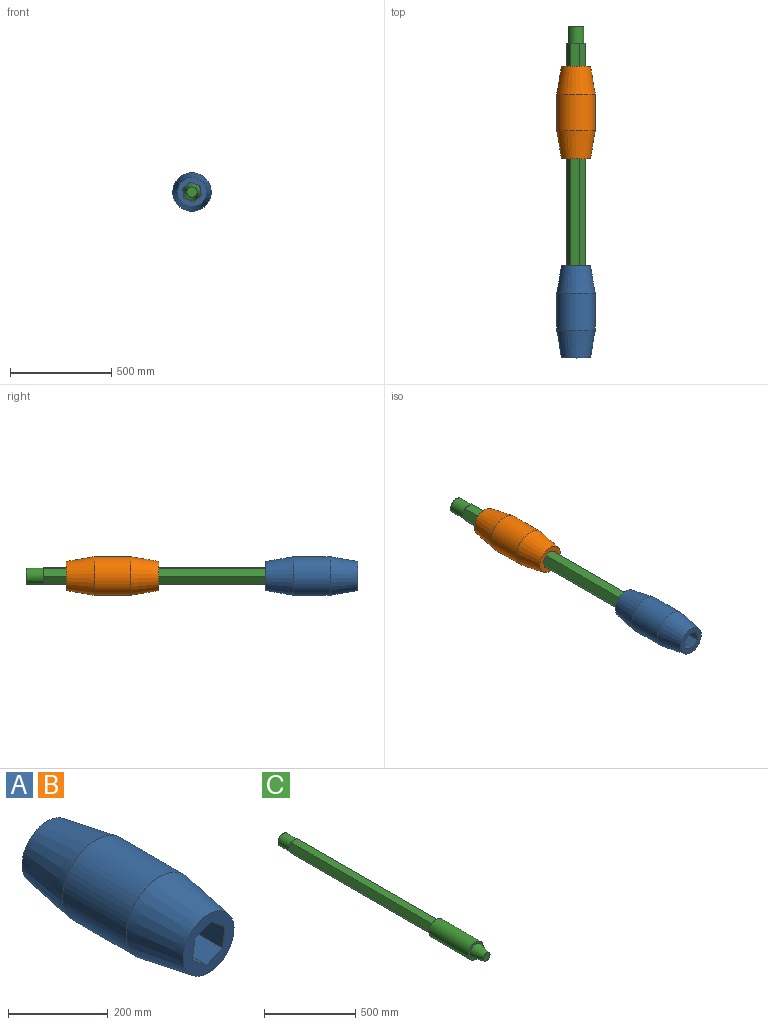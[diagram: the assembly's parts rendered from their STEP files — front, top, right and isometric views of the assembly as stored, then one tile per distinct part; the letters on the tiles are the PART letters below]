
ASSEMBLY  parts=3 mates=2
PART A: 11 faces, bbox 190.5x457.2x190.5 mm
  f0: plane 144.08x144.08mm, normal (0,1,0), area 9802.4mm2, adj f1,f5,f6,f7,f8,f9,f10
  f1: cone r=95.25mm half-angle=9.5deg, axis (0,-1,0), area 73644.5mm2, adj f0,f2
  f2: cylinder r=95.25mm len=190.5mm, axis (0,-1,0), area 108215.6mm2, adj f1,f3
  f3: cone r=95.25mm half-angle=9.5deg, axis (0,1,0), area 73644.5mm2, adj f2,f4
  f4: plane 144.08x144.08mm, normal (0,-1,0), area 9802.4mm2, adj f3,f5,f6,f7,f8,f9,f10
  f5: plane 457.2x49.53mm, normal (0.99,0,-0.14), area 22872.3mm2, adj f0,f4,f6,f10
  f6: plane 457.2x46.41mm, normal (0.37,0,-0.93), area 22872.3mm2, adj f0,f4,f5,f7
  f7: plane 457.2x39.38mm, normal (-0.62,0,-0.79), area 22872.3mm2, adj f0,f4,f6,f8
  f8: plane 457.2x49.53mm, normal (-0.99,0,0.14), area 22872.3mm2, adj f0,f4,f7,f9
  f9: plane 457.2x46.41mm, normal (-0.37,0,0.93), area 22872.3mm2, adj f0,f4,f8,f10
  f10: plane 457.2x39.38mm, normal (0.62,0,0.79), area 22872.3mm2, adj f0,f4,f5,f9
PART B: same geometry as A
PART C: 21 faces, bbox 114.3x1574.8x114.3 mm
  f0: plane 51.34x51.34mm, normal (0,-1,0), area 2070.2mm2, adj f4
  f1: plane 114.3x114.3mm, normal (0,1,0), area 2718.9mm2, adj f2,f11
  f2: cylinder r=57.15mm len=304.8mm, axis (0,-1,0), area 109448.8mm2, adj f1,f3
  f3: plane 114.3x114.3mm, normal (0,-1,0), area 4053.7mm2, adj f2,f4
  f4: cone r=25.67mm half-angle=12.5deg, axis (0,1,0), area 19159.4mm2, adj f0,f3
  f5: plane 1099.82x41.44mm, normal (0.91,0,-0.42), area 50211.5mm2, adj f6,f10,f12,f14,f18
  f6: plane 1099.82x37.31mm, normal (0.82,0,0.58), area 50211.5mm2, adj f5,f7,f12,f14,f15
  f7: plane 1099.82x45.47mm, normal (-0.09,0,1), area 50211.5mm2, adj f6,f8,f12,f15,f16
  f8: plane 1099.82x41.44mm, normal (-0.91,0,0.42), area 50211.5mm2, adj f7,f9,f12,f16,f17
  f9: plane 1099.82x37.31mm, normal (-0.82,0,-0.58), area 50211.5mm2, adj f8,f10,f12,f17,f20
  f10: plane 1099.82x45.47mm, normal (0.09,0,-1), area 50211.5mm2, adj f5,f9,f12,f18,f20
  f11: cylinder r=49mm len=97.99mm, axis (0,1,0), area 54.8mm2, adj f1,f12
  f12: plane 97.99x97.99mm, normal (0,1,0), area 2126.7mm2, adj f5,f6,f7,f8,f9,f10,f11
  f13: plane 79.08x79.08mm, normal (0,1,0), area 4911mm2, adj f19
  f14: plane 39.38x13.15mm, normal (0,1,0), area 84mm2, adj f5,f6,f19
  f15: plane 35.89x18.66mm, normal (0,1,0), area 84mm2, adj f6,f7,f19
  f16: plane 32.32x22.78mm, normal (0,1,0), area 84mm2, adj f7,f8,f19
  f17: plane 39.38x13.15mm, normal (0,1,0), area 84mm2, adj f8,f9,f19
  f18: plane 32.32x22.78mm, normal (0,1,0), area 84mm2, adj f5,f10,f19
  f19: cylinder r=39.54mm len=85.44mm, axis (0,-1,0), area 21224.3mm2, adj f13,f14,f15,f16,f17,f18,f20
  f20: plane 35.89x18.66mm, normal (0,1,0), area 84mm2, adj f9,f10,f19
PLACE A rot(axis=(-1,0,0),180deg) t=(-132.66,-1383.12,-180.43)mm
PLACE B rot(axis=(-1,0,0),180deg) t=(-132.66,-396.93,-180.43)mm
PLACE C rot(axis=(0.39,0.22,-0.89),0deg) t=(-132.66,-715.13,-180.43)mm
MATE slider A.f1 <-> C.f2  axis (0,1,0) through (-132.66,-1203.8,-180.43)mm
MATE slider B.f1 <-> C.f2  axis (0,-1,0) through (-132.66,-674.8,-180.43)mm
